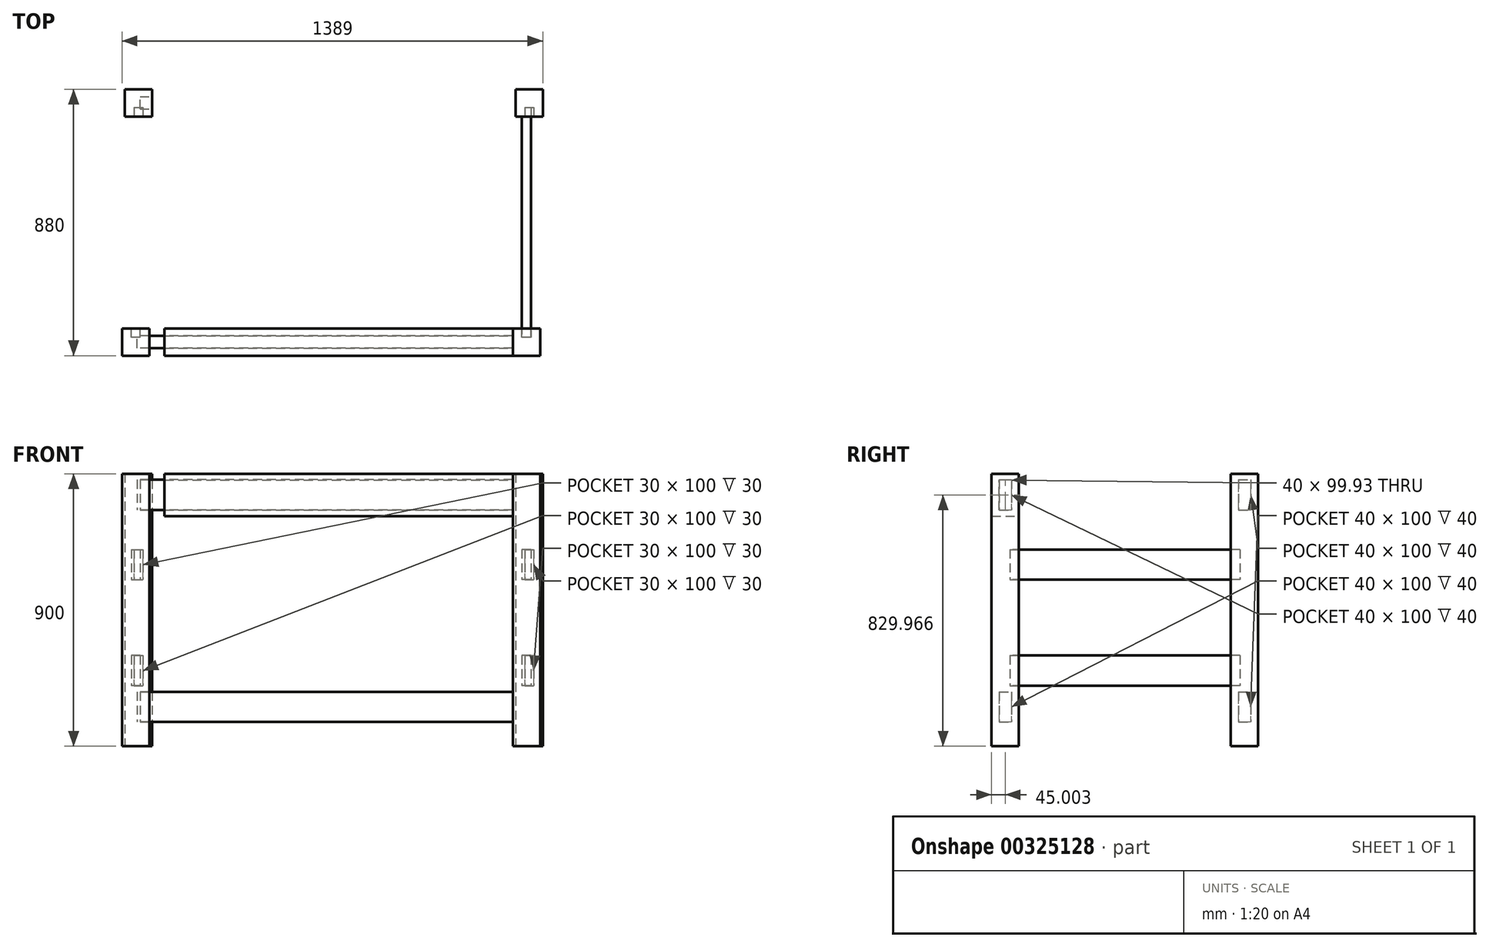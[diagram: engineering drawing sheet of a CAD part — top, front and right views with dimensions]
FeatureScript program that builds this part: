
annotation { "Feature Type Name" : "Feature", "Feature Type Description" : "" }
export const myFeature = defineFeature(function(context is Context, id is Id, definition is map)
    precondition{}
    {
        {
            var Q0;
            Q0=qCreatedBy(makeId("Top.planeOp"),FACE);
            var sketch = newSketch(context, id + "F0", { "sketchPlane" : qUnion([Q0])});
            skLineSegment(sketch, "E0.bottom", {"start": v(-432.8, 264.9) * mm, "end": v(-342.8, 264.9) * mm});
            skLineSegment(sketch, "E0.top", {"start": v(-432.8, 174.9) * mm, "end": v(-342.8, 174.9) * mm});
            skLineSegment(sketch, "E0.left", {"start": v(-432.8, 264.9) * mm, "end": v(-432.8, 174.9) * mm});
            skLineSegment(sketch, "E0.right", {"start": v(-342.8, 264.9) * mm, "end": v(-342.8, 174.9) * mm});
            skLineSegment(sketch, "E1.bottom", {"start": v(-441.8, -525.1) * mm, "end": v(-351.8, -525.1) * mm});
            skLineSegment(sketch, "E1.top", {"start": v(-441.8, -615.1) * mm, "end": v(-351.8, -615.1) * mm});
            skLineSegment(sketch, "E1.left", {"start": v(-441.8, -525.1) * mm, "end": v(-441.8, -615.1) * mm});
            skLineSegment(sketch, "E1.right", {"start": v(-351.8, -525.1) * mm, "end": v(-351.8, -615.1) * mm});
            skLineSegment(sketch, "E2.right", {"start": v(-1123.71, 627.02) * mm, "end": v(-1123.71, 537.02) * mm});
            skLineSegment(sketch, "E3.bottom", {"start": v(857.2, 174.9) * mm, "end": v(947.2, 174.9) * mm});
            skLineSegment(sketch, "E3.top", {"start": v(857.2, 264.9) * mm, "end": v(947.2, 264.9) * mm});
            skLineSegment(sketch, "E3.left", {"start": v(857.2, 174.9) * mm, "end": v(857.2, 264.9) * mm});
            skLineSegment(sketch, "E3.right", {"start": v(947.2, 174.9) * mm, "end": v(947.2, 264.9) * mm});
            skLineSegment(sketch, "E4.bottom", {"start": v(848.2, -525.1) * mm, "end": v(938.2, -525.1) * mm});
            skLineSegment(sketch, "E4.top", {"start": v(848.2, -615.1) * mm, "end": v(938.2, -615.1) * mm});
            skLineSegment(sketch, "E4.left", {"start": v(848.2, -525.1) * mm, "end": v(848.2, -615.1) * mm});
            skLineSegment(sketch, "E4.right", {"start": v(938.2, -525.1) * mm, "end": v(938.2, -615.1) * mm});
            skSolve(sketch);
        }
        {
            var Q0;
            Q0 = qSketchRegion(id + "F0", true);
            extrude(context, id + "F1", {"entities" : qUnion([Q0]), "depth" : 900 * mm});
        }
        {
            var Q0;
            Q0=makeQuery(id+"F1.opExtrude","SWEPT_FACE",FACE,{"disambiguationData":[OSD([sQuery(id+"F0.wireOp",EDGE,"E4.bottom")])]});
            var sketch = newSketch(context, id + "F2", { "sketchPlane" : qUnion([Q0])});
            skLineSegment(sketch, "E5.bottom", {"start": v(-908.2, 650) * mm, "end": v(-878.2, 650) * mm});
            skLineSegment(sketch, "E5.top", {"start": v(-908.2, 550) * mm, "end": v(-878.2, 550) * mm});
            skLineSegment(sketch, "E5.left", {"start": v(-908.2, 650) * mm, "end": v(-908.2, 550) * mm});
            skLineSegment(sketch, "E5.right", {"start": v(-878.2, 650) * mm, "end": v(-878.2, 550) * mm});
            skLineSegment(sketch, "E6.bottom", {"start": v(-908.2, 300) * mm, "end": v(-878.2, 300) * mm});
            skLineSegment(sketch, "E6.top", {"start": v(-908.2, 200) * mm, "end": v(-878.2, 200) * mm});
            skLineSegment(sketch, "E6.left", {"start": v(-908.2, 300) * mm, "end": v(-908.2, 200) * mm});
            skLineSegment(sketch, "E6.right", {"start": v(-878.2, 300) * mm, "end": v(-878.2, 200) * mm});
            skLineSegment(sketch, "E7.bottom", {"start": v(-708.37, 414.18) * mm, "end": v(-745.64, 414.18) * mm});
            skLineSegment(sketch, "E7.top", {"start": v(-708.37, 296.62) * mm, "end": v(-745.64, 296.62) * mm});
            skLineSegment(sketch, "E7.left", {"start": v(-708.37, 414.18) * mm, "end": v(-708.37, 296.62) * mm});
            skLineSegment(sketch, "E7.right", {"start": v(-745.64, 414.18) * mm, "end": v(-745.64, 296.62) * mm});
            skSolve(sketch);
        }
        {
            var Q0;
            Q0=makeQuery(id+"F2.imprint","IMPRINT",FACE,{"disambiguationData":[TD([[makeQuery(id+"F2.imprint","IMPRINT",EDGE,{"derivedFrom":sQuery(id+"F2.wireOp",EDGE,"E5.bottom")}),-1.0]])]});
            var Q1;
            Q1=makeQuery(id+"F2.imprint","IMPRINT",FACE,{"disambiguationData":[TD([[makeQuery(id+"F2.imprint","IMPRINT",EDGE,{"derivedFrom":sQuery(id+"F2.wireOp",EDGE,"E6.bottom")}),-1.0]])]});
            extrude(context, id + "F3", {"entities" : qUnion([Q0, Q1]), "operationType" : NewBodyOperationType.REMOVE, "oppositeDirection" : true, "depth" : 30 * mm});
        }
        {
            var Q0;
            Q0=makeQuery(id+"F1.opExtrude","SWEPT_FACE",FACE,{"disambiguationData":[OSD([sQuery(id+"F0.wireOp",EDGE,"E3.bottom")])]});
            var sketch = newSketch(context, id + "F4", { "sketchPlane" : qUnion([Q0])});
            skLineSegment(sketch, "E8.bottom", {"start": v(887.2, 650) * mm, "end": v(917.2, 650) * mm});
            skLineSegment(sketch, "E8.top", {"start": v(887.2, 550) * mm, "end": v(917.2, 550) * mm});
            skLineSegment(sketch, "E8.left", {"start": v(887.2, 650) * mm, "end": v(887.2, 550) * mm});
            skLineSegment(sketch, "E8.right", {"start": v(917.2, 650) * mm, "end": v(917.2, 550) * mm});
            skLineSegment(sketch, "E9.bottom", {"start": v(887.2, 300) * mm, "end": v(917.2, 300) * mm});
            skLineSegment(sketch, "E9.top", {"start": v(887.2, 200) * mm, "end": v(917.2, 200) * mm});
            skLineSegment(sketch, "E9.left", {"start": v(887.2, 300) * mm, "end": v(887.2, 200) * mm});
            skLineSegment(sketch, "E9.right", {"start": v(917.2, 300) * mm, "end": v(917.2, 200) * mm});
            skSolve(sketch);
        }
        {
            var Q0;
            Q0 = qSketchRegion(id + "F4", true);
            extrude(context, id + "F5", {"entities" : qUnion([Q0]), "operationType" : NewBodyOperationType.REMOVE, "oppositeDirection" : true, "depth" : 30 * mm});
        }
        {
            var Q0;
            Q0=makeQuery(id+"F1.opExtrude","SWEPT_FACE",FACE,{"disambiguationData":[OSD([sQuery(id+"F0.wireOp",EDGE,"E1.bottom")])]});
            var sketch = newSketch(context, id + "F6", { "sketchPlane" : qUnion([Q0])});
            skLineSegment(sketch, "E10.bottom", {"start": v(411.8, 650) * mm, "end": v(381.8, 650) * mm});
            skLineSegment(sketch, "E10.top", {"start": v(411.8, 550) * mm, "end": v(381.8, 550) * mm});
            skLineSegment(sketch, "E10.left", {"start": v(411.8, 650) * mm, "end": v(411.8, 550) * mm});
            skLineSegment(sketch, "E10.right", {"start": v(381.8, 650) * mm, "end": v(381.8, 550) * mm});
            skLineSegment(sketch, "E11.bottom", {"start": v(381.8, 300) * mm, "end": v(411.8, 300) * mm});
            skLineSegment(sketch, "E11.top", {"start": v(381.8, 200) * mm, "end": v(411.8, 200) * mm});
            skLineSegment(sketch, "E11.left", {"start": v(381.8, 300) * mm, "end": v(381.8, 200) * mm});
            skLineSegment(sketch, "E11.right", {"start": v(411.8, 300) * mm, "end": v(411.8, 200) * mm});
            skSolve(sketch);
        }
        {
            var Q0;
            Q0 = qSketchRegion(id + "F6", true);
            extrude(context, id + "F7", {"entities" : qUnion([Q0]), "operationType" : NewBodyOperationType.REMOVE, "oppositeDirection" : true, "depth" : 30 * mm});
        }
        {
            var Q0;
            Q0=makeQuery(id+"F1.opExtrude","SWEPT_FACE",FACE,{"disambiguationData":[OSD([sQuery(id+"F0.wireOp",EDGE,"E0.top")])]});
            var sketch = newSketch(context, id + "F8", { "sketchPlane" : qUnion([Q0])});
            skLineSegment(sketch, "E12.bottom", {"start": v(-402.8, 300) * mm, "end": v(-372.8, 300) * mm});
            skLineSegment(sketch, "E12.top", {"start": v(-402.8, 200) * mm, "end": v(-372.8, 200) * mm});
            skLineSegment(sketch, "E12.left", {"start": v(-402.8, 300) * mm, "end": v(-402.8, 200) * mm});
            skLineSegment(sketch, "E12.right", {"start": v(-372.8, 300) * mm, "end": v(-372.8, 200) * mm});
            skLineSegment(sketch, "E13.bottom", {"start": v(-402.8, 650) * mm, "end": v(-372.8, 650) * mm});
            skLineSegment(sketch, "E13.top", {"start": v(-402.8, 550) * mm, "end": v(-372.8, 550) * mm});
            skLineSegment(sketch, "E13.left", {"start": v(-402.8, 650) * mm, "end": v(-402.8, 550) * mm});
            skLineSegment(sketch, "E13.right", {"start": v(-372.8, 650) * mm, "end": v(-372.8, 550) * mm});
            skSolve(sketch);
        }
        {
            var Q0;
            Q0 = qSketchRegion(id + "F8", true);
            extrude(context, id + "F9", {"entities" : qUnion([Q0]), "operationType" : NewBodyOperationType.REMOVE, "oppositeDirection" : true, "depth" : 30 * mm});
        }
        {
            var Q0;
            Q0=makeQuery(id+"F3.boolean.opBoolean","COPY",FACE,{"derivedFrom":makeQuery(id+"F3.opExtrude","CAP_FACE",FACE,{"disambiguationData":[OSD([sQuery(id+"F2.wireOp",EDGE,"E5.bottom"),sQuery(id+"F2.wireOp",EDGE,"E5.top"),sQuery(id+"F2.wireOp",EDGE,"E5.left"),sQuery(id+"F2.wireOp",EDGE,"E5.right")])],"isStart":false})});
            var Q1;
            Q1=makeQuery(id+"F3.boolean.opBoolean","COPY",FACE,{"derivedFrom":makeQuery(id+"F3.opExtrude","CAP_FACE",FACE,{"disambiguationData":[OSD([sQuery(id+"F2.wireOp",EDGE,"E6.bottom"),sQuery(id+"F2.wireOp",EDGE,"E6.top"),sQuery(id+"F2.wireOp",EDGE,"E6.left"),sQuery(id+"F2.wireOp",EDGE,"E6.right")])],"isStart":false})});
            var Q2;
            Q2=makeQuery(id+"F5.boolean.opBoolean","COPY",FACE,{"derivedFrom":makeQuery(id+"F5.opExtrude","SWEPT_FACE",FACE,{"disambiguationData":[OSD([sQuery(id+"F4.wireOp",EDGE,"E8.left")])]})});
            extrude(context, id + "F10", {"entities" : qUnion([Q0, Q1]), "endBound" : BoundingType.UP_TO_NEXT, "endBoundEntityFace" : qUnion([Q2]), "depth" : 500 * mm});
        }
        {
            var Q0;
            Q0=makeQuery(id+"F1.opExtrude","SWEPT_FACE",FACE,{"disambiguationData":[OSD([sQuery(id+"F0.wireOp",EDGE,"E1.right")])]});
            var sketch = newSketch(context, id + "F11", { "sketchPlane" : qUnion([Q0])});
            skLineSegment(sketch, "E14.bottom", {"start": v(-590.1, 180) * mm, "end": v(-550.1, 180) * mm});
            skLineSegment(sketch, "E14.top", {"start": v(-590.1, 80) * mm, "end": v(-550.1, 80) * mm});
            skLineSegment(sketch, "E14.left", {"start": v(-590.1, 180) * mm, "end": v(-590.1, 80) * mm});
            skLineSegment(sketch, "E14.right", {"start": v(-550.1, 180) * mm, "end": v(-550.1, 80) * mm});
            skLineSegment(sketch, "E15.bottom", {"start": v(-590.1, 880) * mm, "end": v(-550.1, 880) * mm});
            skLineSegment(sketch, "E15.top", {"start": v(-590.1, 780) * mm, "end": v(-550.1, 780) * mm});
            skLineSegment(sketch, "E15.left", {"start": v(-590.1, 880) * mm, "end": v(-590.1, 780) * mm});
            skLineSegment(sketch, "E15.right", {"start": v(-550.1, 880) * mm, "end": v(-550.1, 780) * mm});
            skSolve(sketch);
        }
        {
            var Q0;
            Q0=makeQuery(id+"F11.imprint","IMPRINT",FACE,{"disambiguationData":[TD([[makeQuery(id+"F11.imprint","IMPRINT",EDGE,{"derivedFrom":sQuery(id+"F11.wireOp",EDGE,"E15.bottom")}),-1.0]])]});
            var Q1;
            Q1=makeQuery(id+"F11.imprint","IMPRINT",FACE,{"disambiguationData":[TD([[makeQuery(id+"F11.imprint","IMPRINT",EDGE,{"derivedFrom":sQuery(id+"F11.wireOp",EDGE,"E14.bottom")}),-1.0]])]});
            extrude(context, id + "F12", {"entities" : qUnion([Q0, Q1]), "operationType" : NewBodyOperationType.REMOVE, "oppositeDirection" : true, "depth" : 40 * mm});
        }
        {
            var Q0;
            Q0=makeQuery(id+"F1.opExtrude","SWEPT_FACE",FACE,{"disambiguationData":[OSD([sQuery(id+"F0.wireOp",EDGE,"E0.right")])]});
            var sketch = newSketch(context, id + "F13", { "sketchPlane" : qUnion([Q0])});
            skLineSegment(sketch, "E16.bottom", {"start": v(199.9, 880) * mm, "end": v(239.9, 880) * mm});
            skLineSegment(sketch, "E16.top", {"start": v(199.9, 780) * mm, "end": v(239.9, 780) * mm});
            skLineSegment(sketch, "E16.left", {"start": v(199.9, 880) * mm, "end": v(199.9, 780) * mm});
            skLineSegment(sketch, "E16.right", {"start": v(239.9, 880) * mm, "end": v(239.9, 780) * mm});
            skLineSegment(sketch, "E17.bottom", {"start": v(199.9, 180) * mm, "end": v(239.9, 180) * mm});
            skLineSegment(sketch, "E17.top", {"start": v(199.9, 80) * mm, "end": v(239.9, 80) * mm});
            skLineSegment(sketch, "E17.left", {"start": v(199.9, 180) * mm, "end": v(199.9, 80) * mm});
            skLineSegment(sketch, "E17.right", {"start": v(239.9, 180) * mm, "end": v(239.9, 80) * mm});
            skSolve(sketch);
        }
        {
            var Q0;
            Q0=makeQuery(id+"F13.imprint","IMPRINT",FACE,{"disambiguationData":[TD([[makeQuery(id+"F13.imprint","IMPRINT",EDGE,{"derivedFrom":sQuery(id+"F13.wireOp",EDGE,"E16.bottom")}),-1.0]])]});
            var Q1;
            Q1=makeQuery(id+"F13.imprint","IMPRINT",FACE,{"disambiguationData":[TD([[makeQuery(id+"F13.imprint","IMPRINT",EDGE,{"derivedFrom":sQuery(id+"F13.wireOp",EDGE,"E17.bottom")}),-1.0]])]});
            extrude(context, id + "F14", {"entities" : qUnion([Q0, Q1]), "operationType" : NewBodyOperationType.REMOVE, "oppositeDirection" : true, "depth" : 40 * mm});
        }
        {
            var Q0;
            Q0=makeQuery(id+"F12.boolean.opBoolean","COPY",FACE,{"derivedFrom":makeQuery(id+"F12.opExtrude","CAP_FACE",FACE,{"disambiguationData":[OSD([sQuery(id+"F11.wireOp",EDGE,"E15.bottom"),sQuery(id+"F11.wireOp",EDGE,"E15.top"),sQuery(id+"F11.wireOp",EDGE,"E15.left"),sQuery(id+"F11.wireOp",EDGE,"E15.right")])],"isStart":false})});
            extrude(context, id + "F15", {"entities" : qUnion([Q0]), "endBound" : BoundingType.UP_TO_NEXT, "depth" : 25 * mm});
        }
        {
            var Q0;
            Q0=makeQuery(id+"F12.boolean.opBoolean","COPY",FACE,{"derivedFrom":makeQuery(id+"F12.opExtrude","CAP_FACE",FACE,{"disambiguationData":[OSD([sQuery(id+"F11.wireOp",EDGE,"E14.bottom"),sQuery(id+"F11.wireOp",EDGE,"E14.top"),sQuery(id+"F11.wireOp",EDGE,"E14.left"),sQuery(id+"F11.wireOp",EDGE,"E14.right")])],"isStart":false})});
            extrude(context, id + "F16", {"entities" : qUnion([Q0]), "endBound" : BoundingType.UP_TO_NEXT, "depth" : 25 * mm});
        }
        {
            var Q0;
            Q0=makeQuery(id+"F1.opExtrude","SWEPT_FACE",FACE,{"disambiguationData":[OSD([sQuery(id+"F0.wireOp",EDGE,"E4.left")])]});
            var sketch = newSketch(context, id + "F17", { "sketchPlane" : qUnion([Q0])});
            skLineSegment(sketch, "E18.bottom", {"start": v(525.1, 900) * mm, "end": v(615.1, 900) * mm});
            skLineSegment(sketch, "E18.top", {"start": v(525.1, 879.93) * mm, "end": v(615.1, 879.93) * mm});
            skLineSegment(sketch, "E18.left", {"start": v(525.1, 900) * mm, "end": v(525.1, 879.93) * mm});
            skLineSegment(sketch, "E18.right", {"start": v(615.1, 900) * mm, "end": v(615.1, 879.93) * mm});
            skLineSegment(sketch, "E19.bottom", {"start": v(615.1, 760) * mm, "end": v(525.1, 760) * mm});
            skLineSegment(sketch, "E19.top", {"start": v(615.1, 780) * mm, "end": v(525.1, 780) * mm});
            skLineSegment(sketch, "E19.left", {"start": v(615.1, 760) * mm, "end": v(615.1, 780) * mm});
            skLineSegment(sketch, "E19.right", {"start": v(525.1, 760) * mm, "end": v(525.1, 780) * mm});
            skLineSegment(sketch, "E20.bottom", {"start": v(525.1, 879.93) * mm, "end": v(550.1, 879.93) * mm});
            skLineSegment(sketch, "E20.top", {"start": v(525.1, 780) * mm, "end": v(550.1, 780) * mm});
            skLineSegment(sketch, "E20.left", {"start": v(525.1, 879.93) * mm, "end": v(525.1, 780) * mm});
            skLineSegment(sketch, "E20.right", {"start": v(550.1, 879.93) * mm, "end": v(550.1, 780) * mm});
            skLineSegment(sketch, "E21.bottom", {"start": v(615.1, 780) * mm, "end": v(590.1, 780) * mm});
            skLineSegment(sketch, "E21.top", {"start": v(615.1, 879.93) * mm, "end": v(590.1, 879.93) * mm});
            skLineSegment(sketch, "E21.left", {"start": v(615.1, 780) * mm, "end": v(615.1, 879.93) * mm});
            skLineSegment(sketch, "E21.right", {"start": v(590.1, 780) * mm, "end": v(590.1, 879.93) * mm});
            skSolve(sketch);
        }
        {
            var Q0;
            Q0 = qSketchRegion(id + "F17", true);
            extrude(context, id + "F18", {"entities" : qUnion([Q0]), "depth" : 1150 * mm});
        }
    });
